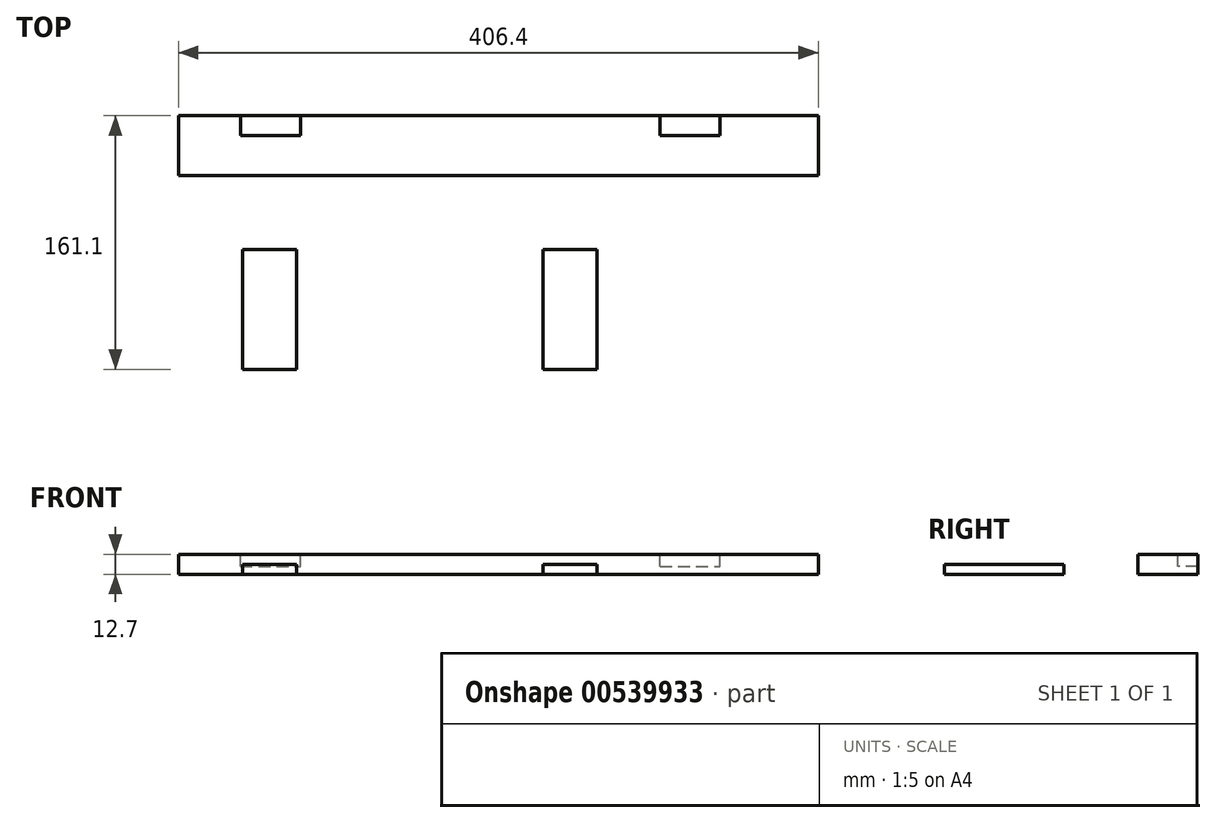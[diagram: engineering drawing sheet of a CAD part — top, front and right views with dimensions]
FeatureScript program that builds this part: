
annotation { "Feature Type Name" : "Feature", "Feature Type Description" : "" }
export const myFeature = defineFeature(function(context is Context, id is Id, definition is map)
    precondition{}
    {
        {
            var Q0;
            Q0=qCreatedBy(makeId("Top.planeOp"),FACE);
            var sketch = newSketch(context, id + "F0", { "sketchPlane" : qUnion([Q0])});
            skLineSegment(sketch, "E0.bottom", {"start": v(-179.72, 54.35) * mm, "end": v(226.68, 54.35) * mm});
            skLineSegment(sketch, "E0.top", {"start": v(-179.72, 16.25) * mm, "end": v(226.68, 16.25) * mm});
            skLineSegment(sketch, "E0.left", {"start": v(-179.72, 54.35) * mm, "end": v(-179.72, 16.25) * mm});
            skLineSegment(sketch, "E0.right", {"start": v(226.68, 54.35) * mm, "end": v(226.68, 16.25) * mm});
            skSolve(sketch);
        }
        {
            var Q0;
            Q0=makeQuery(id+"F0.imprint","IMPRINT",FACE,{"disambiguationData":[TD([[makeQuery(id+"F0.imprint","IMPRINT",EDGE,{"derivedFrom":sQuery(id+"F0.wireOp",EDGE,"E0.bottom")}),-1.0]])]});
            extrude(context, id + "F1", {"entities" : qUnion([Q0]), "depth" : 12.7 * mm, "offsetDistance" : 25.4 * mm});
        }
        {
            var Q0;
            Q0=makeQuery(id+"F1.opExtrude","CAP_FACE",FACE,{"disambiguationData":[OSD([sQuery(id+"F0.wireOp",EDGE,"E0.bottom"),sQuery(id+"F0.wireOp",EDGE,"E0.top"),sQuery(id+"F0.wireOp",EDGE,"E0.left"),sQuery(id+"F0.wireOp",EDGE,"E0.right")])],"isStart":false});
            var sketch = newSketch(context, id + "F2", { "sketchPlane" : qUnion([Q0])});
            skLineSegment(sketch, "E1", {"start": v(-140.3, 54.35) * mm, "end": v(-140.3, 41.65) * mm});
            skLineSegment(sketch, "E2", {"start": v(-102.2, 41.65) * mm, "end": v(-102.2, 54.35) * mm});
            skLineSegment(sketch, "E3", {"start": v(-140.3, 41.65) * mm, "end": v(-102.2, 41.65) * mm});
            skLineSegment(sketch, "E4", {"start": v(126.18, 54.35) * mm, "end": v(126.18, 41.65) * mm});
            skLineSegment(sketch, "E5", {"start": v(126.18, 41.65) * mm, "end": v(164.28, 41.65) * mm});
            skLineSegment(sketch, "E6", {"start": v(164.28, 41.65) * mm, "end": v(164.28, 54.35) * mm});
            skSolve(sketch);
        }
        {
            var Q0;
            {var subQ0=sQuery(id+"F2.wireOp",EDGE,"E1");Q0=makeQuery(id+"F2.imprint","IMPRINT",FACE,{"disambiguationData":[TD([[makeQuery(id+"F2.imprint","IMPRINT",EDGE,{"derivedFrom":subQ0}),1.0]])]});}
            var Q1;
            {var subQ0=sQuery(id+"F2.wireOp",EDGE,"E4");Q1=makeQuery(id+"F2.imprint","IMPRINT",FACE,{"disambiguationData":[TD([[makeQuery(id+"F2.imprint","IMPRINT",EDGE,{"derivedFrom":subQ0}),1.0]])]});}
            extrude(context, id + "F3", {"entities" : qUnion([Q0, Q1]), "operationType" : NewBodyOperationType.REMOVE, "oppositeDirection" : true, "depth" : 7.62 * mm, "offsetDistance" : 25.4 * mm});
        }
        {
            var Q0;
            Q0=qCreatedBy(makeId("Top.planeOp"),FACE);
            var sketch = newSketch(context, id + "F4", { "sketchPlane" : qUnion([Q0])});
            skLineSegment(sketch, "E7.bottom", {"start": v(-138.89, -30.55) * mm, "end": v(-104.6, -30.55) * mm});
            skLineSegment(sketch, "E7.top", {"start": v(-138.89, -106.75) * mm, "end": v(-104.6, -106.75) * mm});
            skLineSegment(sketch, "E7.left", {"start": v(-138.89, -30.55) * mm, "end": v(-138.89, -106.75) * mm});
            skLineSegment(sketch, "E7.right", {"start": v(-104.6, -30.55) * mm, "end": v(-104.6, -106.75) * mm});
            skLineSegment(sketch, "E8.bottom", {"start": v(51.98, -30.55) * mm, "end": v(86.27, -30.55) * mm});
            skLineSegment(sketch, "E8.top", {"start": v(51.98, -106.75) * mm, "end": v(86.27, -106.75) * mm});
            skLineSegment(sketch, "E8.left", {"start": v(51.98, -30.55) * mm, "end": v(51.98, -106.75) * mm});
            skLineSegment(sketch, "E8.right", {"start": v(86.27, -30.55) * mm, "end": v(86.27, -106.75) * mm});
            skSolve(sketch);
        }
        {
            var Q0;
            Q0 = qSketchRegion(id + "F4", true);
            extrude(context, id + "F5", {"entities" : qUnion([Q0]), "depth" : 6.35 * mm, "offsetDistance" : 25.4 * mm});
        }
    });
